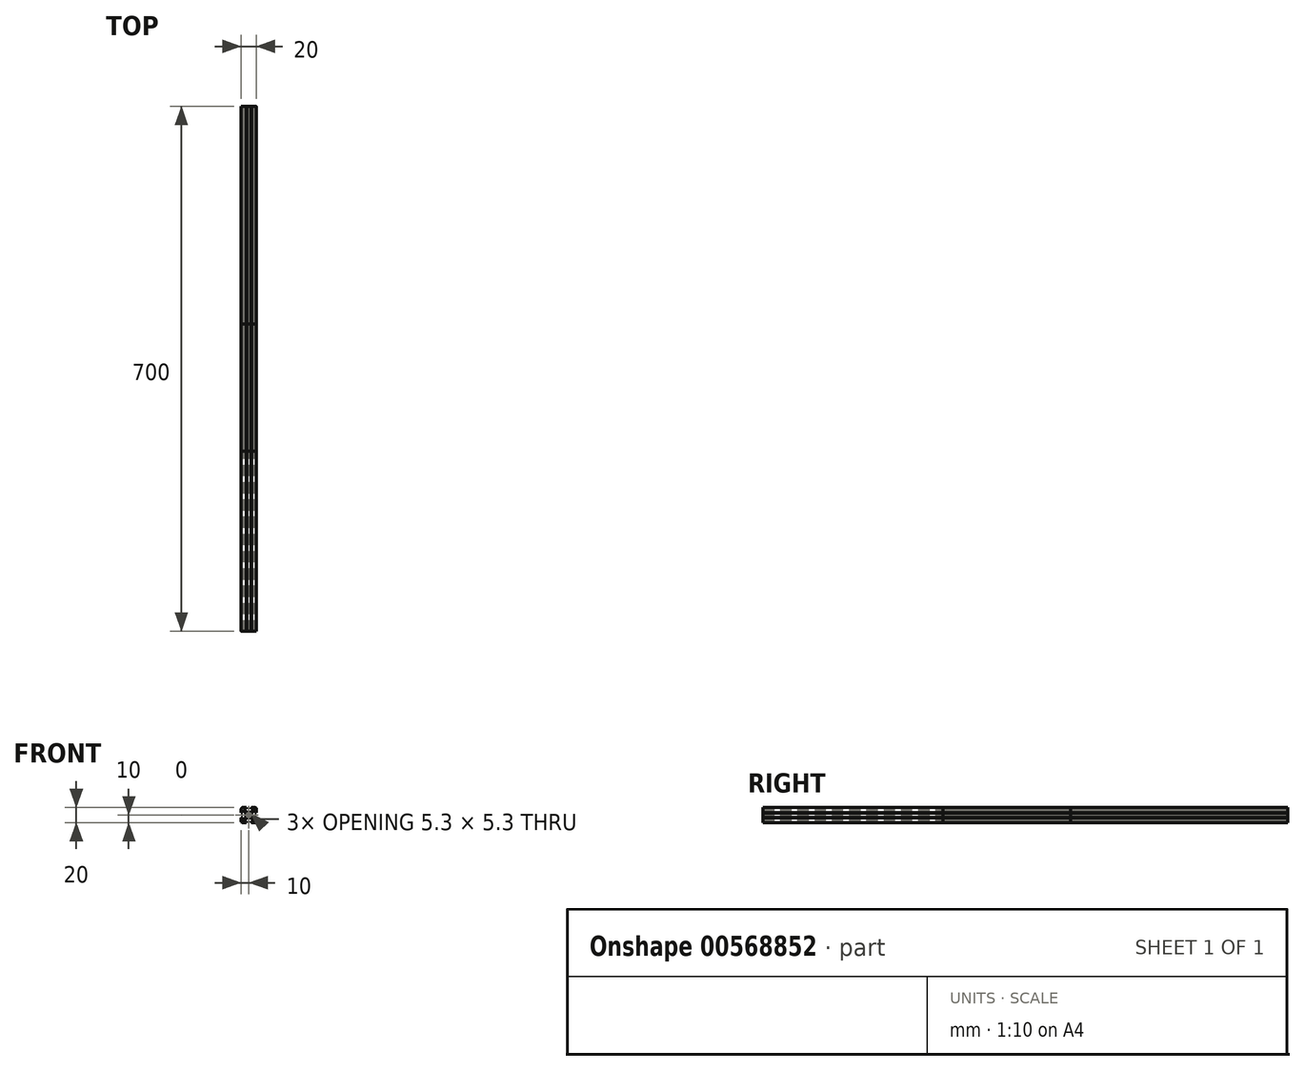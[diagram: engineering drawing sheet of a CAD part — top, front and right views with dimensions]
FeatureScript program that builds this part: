
annotation { "Feature Type Name" : "Feature", "Feature Type Description" : "" }
export const myFeature = defineFeature(function(context is Context, id is Id, definition is map)
    precondition{}
    {
        {
            var Q0;
            Q0=qCreatedBy(makeId("Front.planeOp"),FACE);
            var sketch = newSketch(context, id + "F0", { "sketchPlane" : qUnion([Q0])});
            skLineSegment(sketch, "E0", {"start": v(-12.6, 0) * mm, "end": v(14.19, 0) * mm, "construction": true});
            skLineSegment(sketch, "E1", {"start": v(0, 11.69) * mm, "end": v(0, -18.72) * mm, "construction": true});
            skLineSegment(sketch, "E2", {"start": v(-11.4, 11.4) * mm, "end": v(13.4, -13.4) * mm, "construction": true});
            skLineSegment(sketch, "E3", {"start": v(-2.22, 1.16) * mm, "end": v(-2.65, 1.6) * mm});
            skArc(sketch, "E4.converted", {"start": v(-2.22, 1.16) * mm, "mid": v(-2.5, 0) * mm, "end": v(-2.22, -1.16) * mm});
            skLineSegment(sketch, "E5", {"start": v(-3.9, 2.84) * mm, "end": v(-6.56, 5.5) * mm});
            skLineSegment(sketch, "E6", {"start": v(-8.2, 5.5) * mm, "end": v(-8.2, 3.1) * mm});
            skLineSegment(sketch, "E7", {"start": v(-8.2, 3.1) * mm, "end": v(-9.5, 3.1) * mm});
            skLineSegment(sketch, "E8", {"start": v(-10, 3.6) * mm, "end": v(-10, 8.5) * mm});
            skLineSegment(sketch, "E9", {"start": v(-10, 3.6) * mm, "end": v(-9.5, 3.6) * mm});
            skLineSegment(sketch, "E10", {"start": v(-9.5, 3.6) * mm, "end": v(-9.5, 3.1) * mm});
            skLineSegment(sketch, "E11", {"start": v(-8.2, 5.5) * mm, "end": v(-6.56, 5.5) * mm});
            skArc(sketch, "E12", {"start": v(-8.5, 10) * mm, "mid": v(-9.56, 9.56) * mm, "end": v(-10, 8.5) * mm});
            skLineSegment(sketch, "E13.MirrorCS", {"start": v(-1.16, 2.22) * mm, "end": v(-1.6, 2.65) * mm});
            skLineSegment(sketch, "E14.MirrorCS", {"start": v(-2.84, 3.9) * mm, "end": v(-5.5, 6.56) * mm});
            skLineSegment(sketch, "E15.MirrorCS", {"start": v(-5.5, 8.2) * mm, "end": v(-5.5, 6.56) * mm});
            skLineSegment(sketch, "E16.MirrorCS", {"start": v(-5.5, 8.2) * mm, "end": v(-3.1, 8.2) * mm});
            skLineSegment(sketch, "E17.MirrorCS", {"start": v(-3.1, 8.2) * mm, "end": v(-3.1, 9.5) * mm});
            skLineSegment(sketch, "E18.MirrorCS", {"start": v(-3.6, 9.5) * mm, "end": v(-3.1, 9.5) * mm});
            skLineSegment(sketch, "E19.MirrorCS", {"start": v(-3.6, 10) * mm, "end": v(-3.6, 9.5) * mm});
            skLineSegment(sketch, "E20.MirrorCS", {"start": v(-3.6, 10) * mm, "end": v(-8.5, 10) * mm});
            skLineSegment(sketch, "E21.MirrorCS", {"start": v(1.16, 2.22) * mm, "end": v(1.6, 2.65) * mm});
            skLineSegment(sketch, "E22.MirrorCS", {"start": v(2.22, 1.16) * mm, "end": v(2.65, 1.6) * mm});
            skLineSegment(sketch, "E23.MirrorCS", {"start": v(2.84, 3.9) * mm, "end": v(5.5, 6.56) * mm});
            skLineSegment(sketch, "E24.MirrorCS", {"start": v(3.9, 2.84) * mm, "end": v(6.56, 5.5) * mm});
            skLineSegment(sketch, "E25.MirrorCS", {"start": v(5.5, 8.2) * mm, "end": v(5.5, 6.56) * mm});
            skLineSegment(sketch, "E26.MirrorCS", {"start": v(8.2, 5.5) * mm, "end": v(6.56, 5.5) * mm});
            skLineSegment(sketch, "E27.MirrorCS", {"start": v(5.5, 8.2) * mm, "end": v(3.1, 8.2) * mm});
            skLineSegment(sketch, "E28.MirrorCS", {"start": v(8.2, 5.5) * mm, "end": v(8.2, 3.1) * mm});
            skLineSegment(sketch, "E29.MirrorCS", {"start": v(3.1, 8.2) * mm, "end": v(3.1, 9.5) * mm});
            skLineSegment(sketch, "E30.MirrorCS", {"start": v(8.2, 3.1) * mm, "end": v(9.5, 3.1) * mm});
            skLineSegment(sketch, "E31.MirrorCS", {"start": v(9.5, 3.6) * mm, "end": v(9.5, 3.1) * mm});
            skLineSegment(sketch, "E32.MirrorCS", {"start": v(10, 3.6) * mm, "end": v(9.5, 3.6) * mm});
            skLineSegment(sketch, "E33.MirrorCS", {"start": v(10, 3.6) * mm, "end": v(10, 8.5) * mm});
            skLineSegment(sketch, "E34.MirrorCS", {"start": v(3.6, 9.5) * mm, "end": v(3.1, 9.5) * mm});
            skLineSegment(sketch, "E35.MirrorCS", {"start": v(3.6, 10) * mm, "end": v(3.6, 9.5) * mm});
            skLineSegment(sketch, "E36.MirrorCS", {"start": v(3.6, 10) * mm, "end": v(8.5, 10) * mm});
            skArc(sketch, "E37.MirrorCS", {"start": v(8.5, 10) * mm, "mid": v(9.56, 9.56) * mm, "end": v(10, 8.5) * mm});
            skArc(sketch, "E38.MirrorCS", {"start": v(2.22, 1.16) * mm, "mid": v(2.5, 0) * mm, "end": v(2.22, -1.16) * mm});
            skArc(sketch, "E39.MirrorCS", {"start": v(-1.16, 2.22) * mm, "mid": v(0, 2.5) * mm, "end": v(1.16, 2.22) * mm});
            skLineSegment(sketch, "E40.MirrorCS", {"start": v(2.22, -1.16) * mm, "end": v(2.65, -1.6) * mm});
            skLineSegment(sketch, "E41.MirrorCS", {"start": v(1.16, -2.22) * mm, "end": v(1.6, -2.65) * mm});
            skArc(sketch, "E42.MirrorCS", {"start": v(-1.16, -2.22) * mm, "mid": v(0, -2.5) * mm, "end": v(1.16, -2.22) * mm});
            skLineSegment(sketch, "E43.MirrorCS", {"start": v(-1.16, -2.22) * mm, "end": v(-1.6, -2.65) * mm});
            skLineSegment(sketch, "E44.MirrorCS", {"start": v(-2.22, -1.16) * mm, "end": v(-2.65, -1.6) * mm});
            skLineSegment(sketch, "E45.MirrorCS", {"start": v(3.9, -2.84) * mm, "end": v(6.56, -5.5) * mm});
            skLineSegment(sketch, "E46.MirrorCS", {"start": v(2.84, -3.9) * mm, "end": v(5.5, -6.56) * mm});
            skLineSegment(sketch, "E47.MirrorCS", {"start": v(8.2, -5.5) * mm, "end": v(6.56, -5.5) * mm});
            skLineSegment(sketch, "E48.MirrorCS", {"start": v(8.2, -5.5) * mm, "end": v(8.2, -3.1) * mm});
            skLineSegment(sketch, "E49.MirrorCS", {"start": v(8.2, -3.1) * mm, "end": v(9.5, -3.1) * mm});
            skLineSegment(sketch, "E50.MirrorCS", {"start": v(9.5, -3.6) * mm, "end": v(9.5, -3.1) * mm});
            skLineSegment(sketch, "E51.MirrorCS", {"start": v(10, -3.6) * mm, "end": v(9.5, -3.6) * mm});
            skLineSegment(sketch, "E52.MirrorCS", {"start": v(10, -3.6) * mm, "end": v(10, -8.5) * mm});
            skArc(sketch, "E53.MirrorCS", {"start": v(8.5, -10) * mm, "mid": v(9.56, -9.56) * mm, "end": v(10, -8.5) * mm});
            skLineSegment(sketch, "E54.MirrorCS", {"start": v(3.6, -10) * mm, "end": v(8.5, -10) * mm});
            skLineSegment(sketch, "E55.MirrorCS", {"start": v(3.6, -10) * mm, "end": v(3.6, -9.5) * mm});
            skLineSegment(sketch, "E56.MirrorCS", {"start": v(3.6, -9.5) * mm, "end": v(3.1, -9.5) * mm});
            skLineSegment(sketch, "E57.MirrorCS", {"start": v(3.1, -8.2) * mm, "end": v(3.1, -9.5) * mm});
            skLineSegment(sketch, "E58.MirrorCS", {"start": v(5.5, -8.2) * mm, "end": v(3.1, -8.2) * mm});
            skLineSegment(sketch, "E59.MirrorCS", {"start": v(5.5, -8.2) * mm, "end": v(5.5, -6.56) * mm});
            skLineSegment(sketch, "E60.MirrorCS", {"start": v(-2.84, -3.9) * mm, "end": v(-5.5, -6.56) * mm});
            skLineSegment(sketch, "E61.MirrorCS", {"start": v(-5.5, -8.2) * mm, "end": v(-5.5, -6.56) * mm});
            skLineSegment(sketch, "E62.MirrorCS", {"start": v(-5.5, -8.2) * mm, "end": v(-3.1, -8.2) * mm});
            skLineSegment(sketch, "E63.MirrorCS", {"start": v(-3.1, -8.2) * mm, "end": v(-3.1, -9.5) * mm});
            skLineSegment(sketch, "E64.MirrorCS", {"start": v(-3.6, -9.5) * mm, "end": v(-3.1, -9.5) * mm});
            skLineSegment(sketch, "E65.MirrorCS", {"start": v(-3.6, -10) * mm, "end": v(-3.6, -9.5) * mm});
            skLineSegment(sketch, "E66.MirrorCS", {"start": v(-3.6, -10) * mm, "end": v(-8.5, -10) * mm});
            skArc(sketch, "E67.MirrorCS", {"start": v(-8.5, -10) * mm, "mid": v(-9.56, -9.56) * mm, "end": v(-10, -8.5) * mm});
            skLineSegment(sketch, "E68.MirrorCS", {"start": v(-10, -3.6) * mm, "end": v(-10, -8.5) * mm});
            skLineSegment(sketch, "E69.MirrorCS", {"start": v(-10, -3.6) * mm, "end": v(-9.5, -3.6) * mm});
            skLineSegment(sketch, "E70.MirrorCS", {"start": v(-9.5, -3.6) * mm, "end": v(-9.5, -3.1) * mm});
            skLineSegment(sketch, "E71.MirrorCS", {"start": v(-8.2, -3.1) * mm, "end": v(-9.5, -3.1) * mm});
            skLineSegment(sketch, "E72.MirrorCS", {"start": v(-8.2, -5.5) * mm, "end": v(-8.2, -3.1) * mm});
            skLineSegment(sketch, "E73.MirrorCS", {"start": v(-8.2, -5.5) * mm, "end": v(-6.56, -5.5) * mm});
            skLineSegment(sketch, "E74.MirrorCS", {"start": v(-3.9, -2.84) * mm, "end": v(-6.56, -5.5) * mm});
            skLineSegment(sketch, "E75", {"start": v(-3.9, 2.84) * mm, "end": v(-3.9, -2.84) * mm});
            skLineSegment(sketch, "E76", {"start": v(-2.84, 3.9) * mm, "end": v(2.84, 3.9) * mm});
            skLineSegment(sketch, "E77", {"start": v(3.9, 2.84) * mm, "end": v(3.9, -2.84) * mm});
            skLineSegment(sketch, "E78", {"start": v(2.84, -3.9) * mm, "end": v(-2.84, -3.9) * mm});
            skLineSegment(sketch, "E79", {"start": v(-2.65, -1.6) * mm, "end": v(-1.6, -2.65) * mm});
            skLineSegment(sketch, "E80", {"start": v(1.6, -2.65) * mm, "end": v(2.65, -1.6) * mm});
            skLineSegment(sketch, "E81", {"start": v(2.65, 1.6) * mm, "end": v(1.6, 2.65) * mm});
            skLineSegment(sketch, "E82", {"start": v(-1.6, 2.65) * mm, "end": v(-2.65, 1.6) * mm});
            skSolve(sketch);
        }
        {
            var Q0;
            Q0 = qSketchRegion(id + "F0", true);
            extrude(context, id + "F1", {"entities" : qUnion([Q0]), "depth" : 460 * mm, "offsetDistance" : 25 * mm});
        }
        {
            var Q0;
            Q0 = qSketchRegion(id + "F0", true);
            extrude(context, id + "F2", {"entities" : qUnion([Q0]), "depth" : 700 * mm, "offsetDistance" : 25 * mm});
        }
        {
            var Q0;
            Q0 = qSketchRegion(id + "F0", true);
            extrude(context, id + "F3", {"entities" : qUnion([Q0]), "depth" : 290 * mm, "offsetDistance" : 25 * mm});
        }
    });
